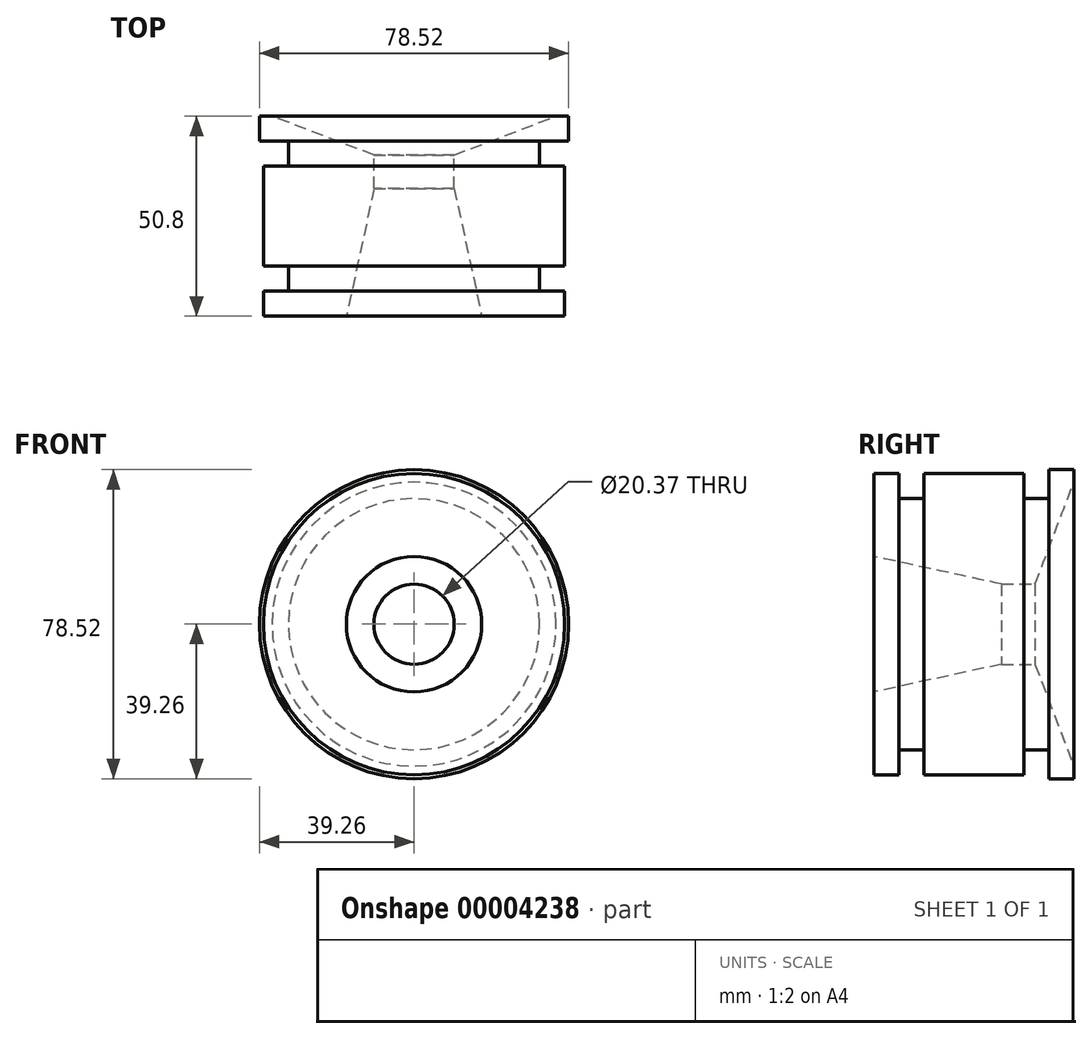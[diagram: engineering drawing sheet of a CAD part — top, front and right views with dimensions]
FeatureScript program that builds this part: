
annotation { "Feature Type Name" : "Feature", "Feature Type Description" : "" }
export const myFeature = defineFeature(function(context is Context, id is Id, definition is map)
    precondition{}
    {
        {
            var Q0;
            Q0=qCreatedBy(makeId("Top.planeOp"),FACE);
            var sketch = newSketch(context, id + "F0", { "sketchPlane" : qUnion([Q0])});
            skLineSegment(sketch, "E0", {"start": v(-38.26, -0.87) * mm, "end": v(-38.26, 5.48) * mm});
            skLineSegment(sketch, "E1", {"start": v(-38.26, 5.48) * mm, "end": v(-31.9, 5.48) * mm});
            skLineSegment(sketch, "E2", {"start": v(-31.9, 5.48) * mm, "end": v(-31.9, 11.83) * mm});
            skLineSegment(sketch, "E3", {"start": v(-31.9, 11.83) * mm, "end": v(-38.26, 11.83) * mm});
            skLineSegment(sketch, "E4", {"start": v(-38.26, 11.83) * mm, "end": v(-38.26, 37.23) * mm});
            skLineSegment(sketch, "E5", {"start": v(-38.26, 37.23) * mm, "end": v(-31.9, 37.23) * mm});
            skLineSegment(sketch, "E6", {"start": v(-31.9, 37.23) * mm, "end": v(-31.9, 43.58) * mm});
            skLineSegment(sketch, "E7", {"start": v(-31.9, 43.58) * mm, "end": v(-39.26, 43.58) * mm});
            skLineSegment(sketch, "E8", {"start": v(-39.26, 43.58) * mm, "end": v(-39.26, 49.93) * mm});
            skLineSegment(sketch, "E9", {"start": v(-39.26, 49.93) * mm, "end": v(-36.08, 49.93) * mm});
            skLineSegment(sketch, "E10", {"start": v(-36.08, 49.93) * mm, "end": v(-10.18, 40.07) * mm});
            skLineSegment(sketch, "E11", {"start": v(-10.18, 40.07) * mm, "end": v(-10.18, 31.55) * mm});
            skLineSegment(sketch, "E12", {"start": v(-10.18, 31.55) * mm, "end": v(-17.2, -0.87) * mm});
            skLineSegment(sketch, "E13", {"start": v(-38.26, -0.87) * mm, "end": v(-17.2, -0.87) * mm});
            skLineSegment(sketch, "E14", {"start": v(0, 51.65) * mm, "end": v(0, 0) * mm});
            skSolve(sketch);
        }
        {
            var Q0;
            Q0=makeQuery(id+"F0.imprint","IMPRINT",FACE,{"disambiguationData":[TD([[makeQuery(id+"F0.imprint","IMPRINT",EDGE,{"derivedFrom":sQuery(id+"F0.wireOp",EDGE,"E0")}),-1.0]])]});
            var Q1;
            Q1=sQuery(id+"F0.wireOp",EDGE,"E14");
            revolve(context, id + "F1", {"entities" : qUnion([Q0]), "axis" : qUnion([Q1]), "revolveType" : RevolveType.FULL});
        }
    });
